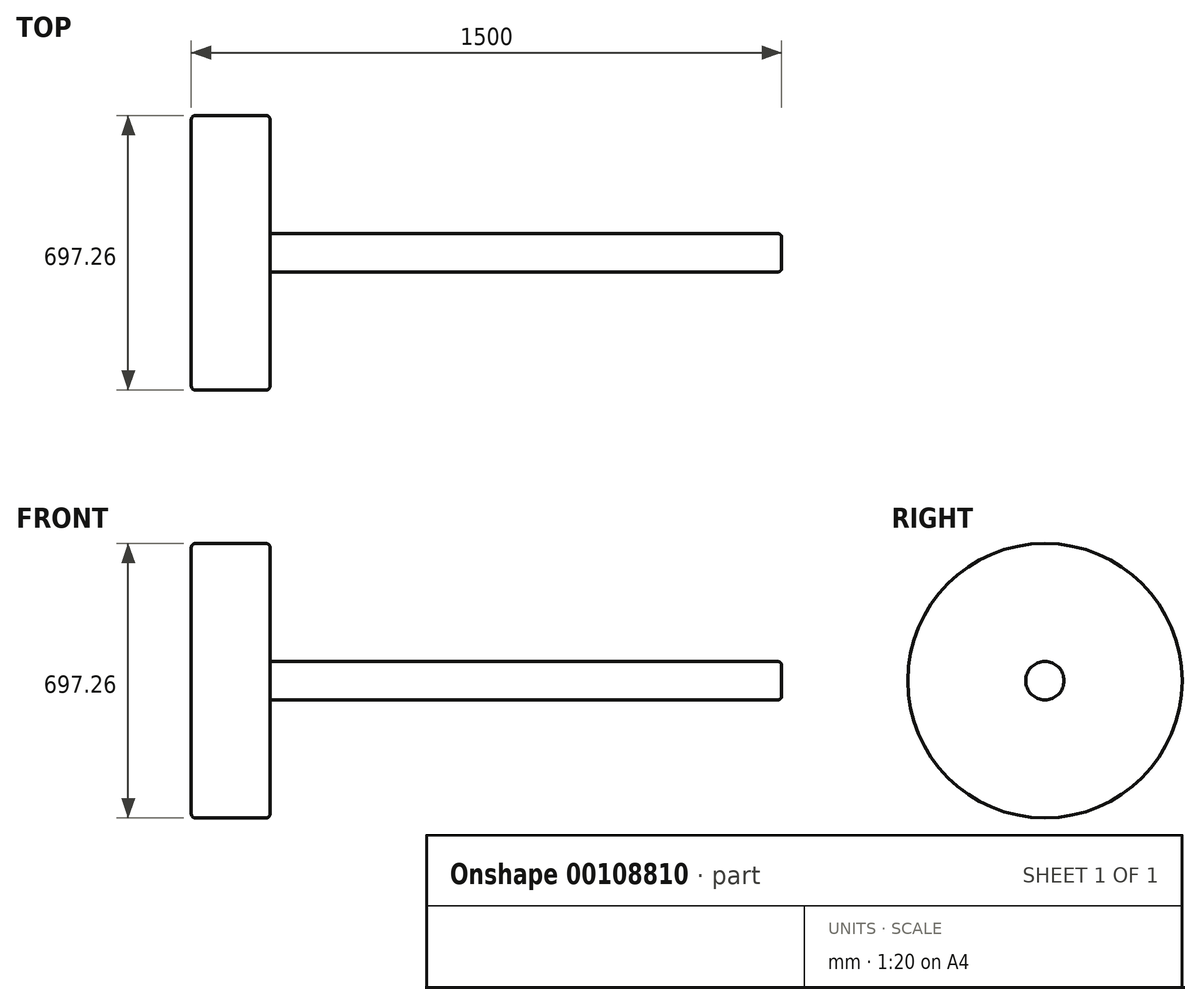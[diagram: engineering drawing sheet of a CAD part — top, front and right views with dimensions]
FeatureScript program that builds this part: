
annotation { "Feature Type Name" : "Feature", "Feature Type Description" : "" }
export const myFeature = defineFeature(function(context is Context, id is Id, definition is map)
    precondition{}
    {
        {
            var Q0;
            Q0=qCreatedBy(makeId("Front.planeOp"),FACE);
            var sketch = newSketch(context, id + "F0", { "sketchPlane" : qUnion([Q0])});
            skLineSegment(sketch, "E0", {"start": v(-171.5, 0) * mm, "end": v(-171.5, 338.63) * mm});
            skLineSegment(sketch, "E1", {"start": v(-161.5, 348.63) * mm, "end": v(18.5, 348.63) * mm});
            skLineSegment(sketch, "E2", {"start": v(28.5, 338.63) * mm, "end": v(28.5, 48.63) * mm});
            skLineSegment(sketch, "E3", {"start": v(28.5, 48.63) * mm, "end": v(1318.5, 48.63) * mm});
            skLineSegment(sketch, "E4", {"start": v(1328.5, 38.63) * mm, "end": v(1328.5, 0) * mm});
            skLineSegment(sketch, "E5", {"start": v(1328.5, 0) * mm, "end": v(-171.5, 0) * mm});
            skPoint(sketch, "E6.visualSharp", {"position": v(1328.5, 48.63) * mm});
            skArc(sketch, "E6.filletArc", {"start": v(1328.5, 38.63) * mm, "mid": v(1325.57, 45.7) * mm, "end": v(1318.5, 48.63) * mm});
            skPoint(sketch, "E7.visualSharp", {"position": v(28.5, 348.63) * mm});
            skArc(sketch, "E7.filletArc", {"start": v(28.5, 338.63) * mm, "mid": v(25.57, 345.7) * mm, "end": v(18.5, 348.63) * mm});
            skPoint(sketch, "E8.visualSharp", {"position": v(-171.5, 348.63) * mm});
            skArc(sketch, "E8.filletArc", {"start": v(-161.5, 348.63) * mm, "mid": v(-168.57, 345.7) * mm, "end": v(-171.5, 338.63) * mm});
            skSolve(sketch);
        }
        {
            var Q0;
            Q0 = qSketchRegion(id + "F0", true);
            var Q1;
            Q1=sQuery(id+"F0.wireOp",EDGE,"E5");
            revolve(context, id + "F1", {"entities" : qUnion([Q0]), "axis" : qUnion([Q1]), "revolveType" : RevolveType.FULL});
        }
    });
